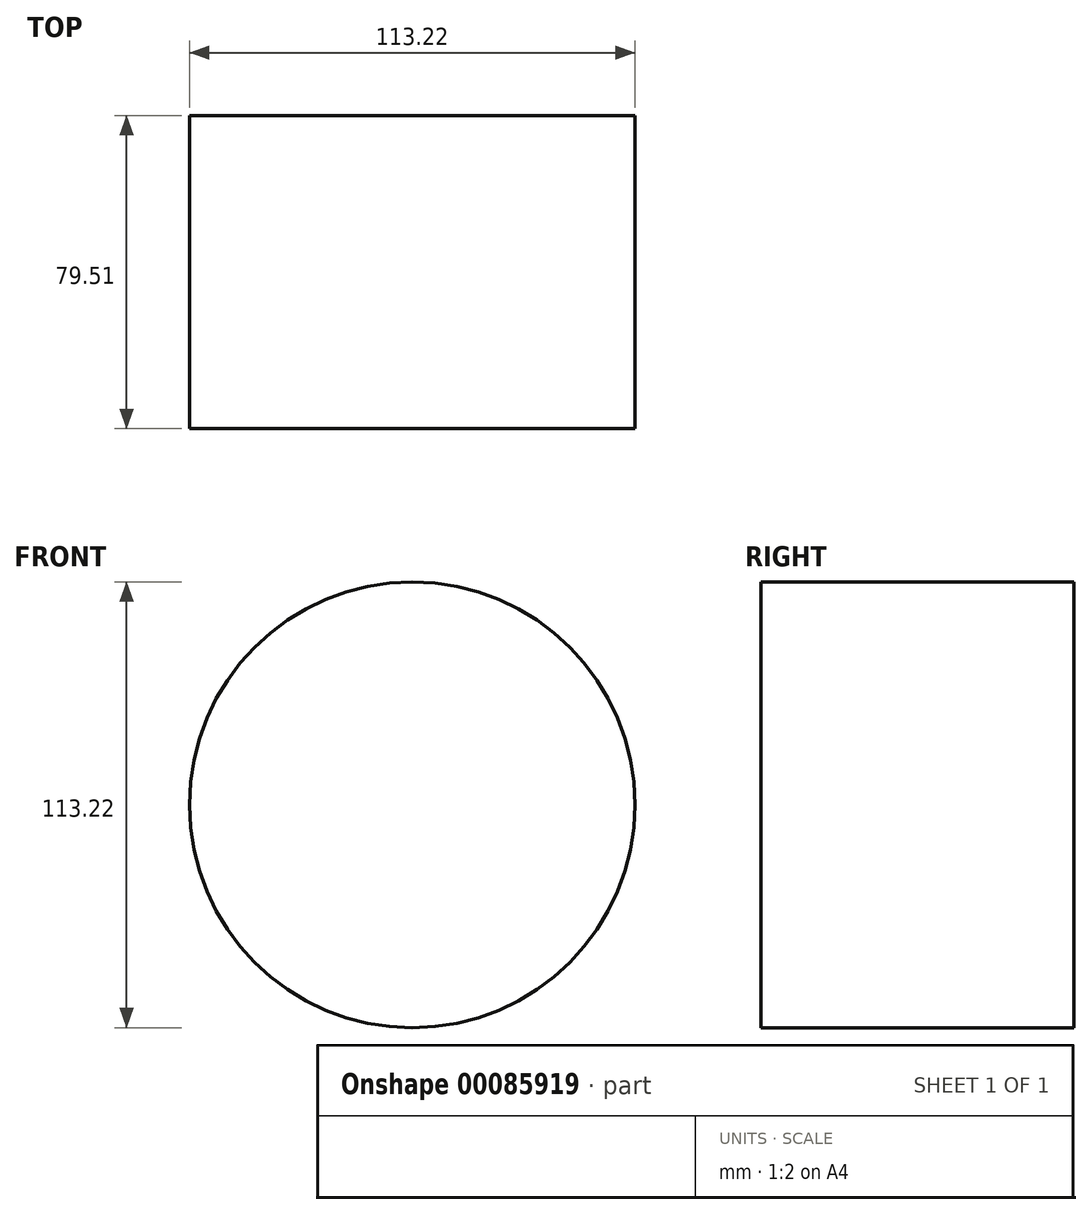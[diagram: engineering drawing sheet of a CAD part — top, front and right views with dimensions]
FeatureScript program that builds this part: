
annotation { "Feature Type Name" : "Feature", "Feature Type Description" : "" }
export const myFeature = defineFeature(function(context is Context, id is Id, definition is map)
    precondition{}
    {
        {
            var Q0;
            Q0=qCreatedBy(makeId("Front.planeOp"),FACE);
            var sketch = newSketch(context, id + "F0", { "sketchPlane" : qUnion([Q0])});
            skCircle(sketch, "E0", {"center": v(0, 0) * mm, "radius": 56.61 * mm});
            skSolve(sketch);
        }
        {
            var Q0;
            Q0 = qSketchRegion(id + "F0", true);
            extrude(context, id + "F1", {"entities" : qUnion([Q0]), "depth" : 79.51 * mm});
        }
    });
